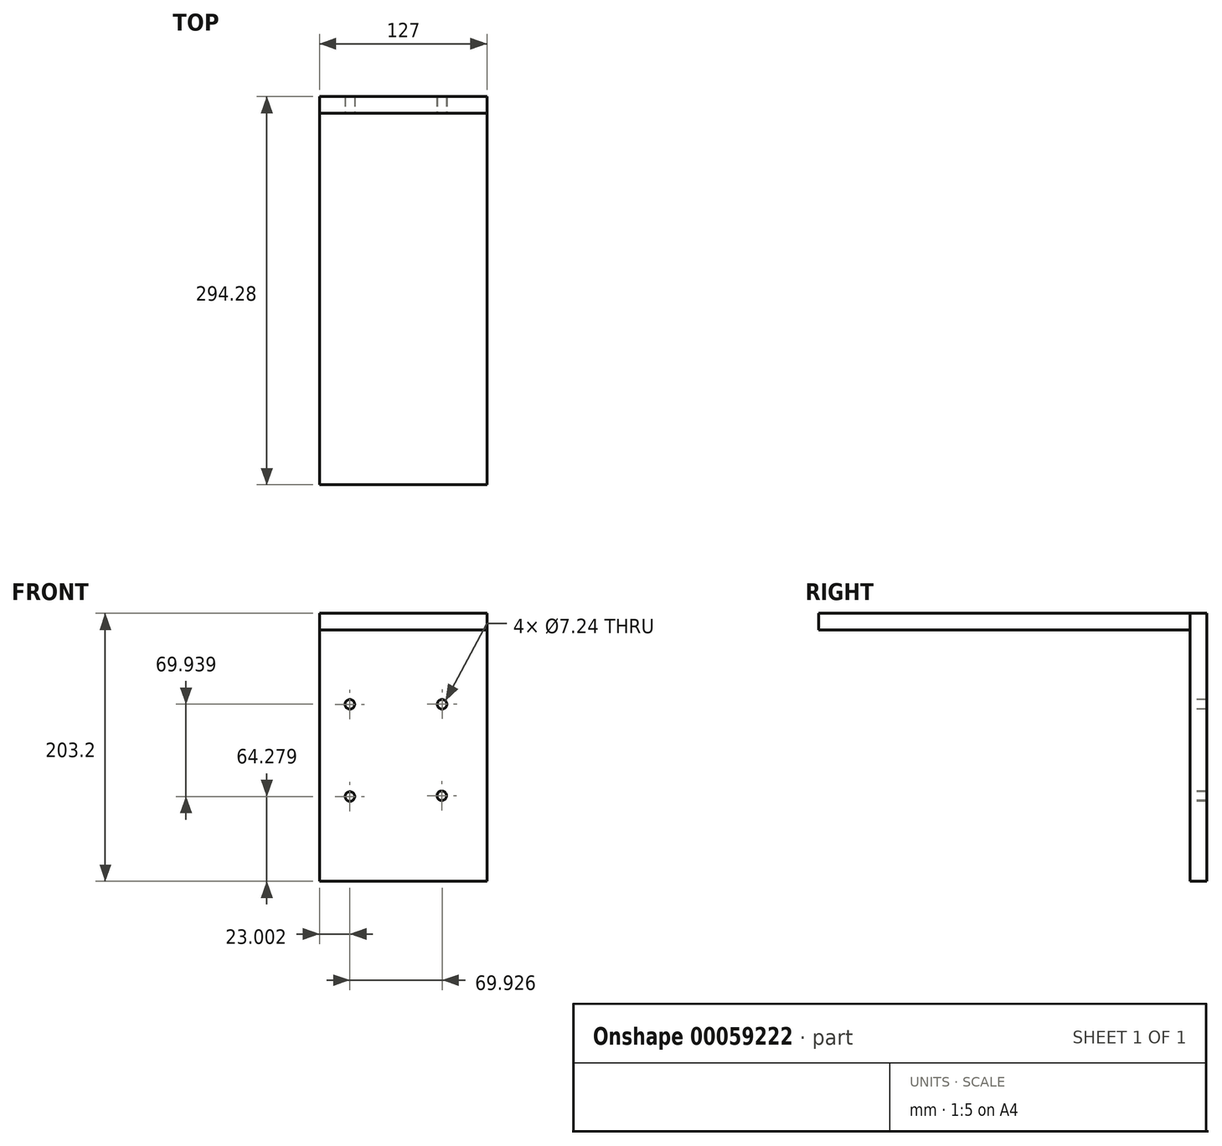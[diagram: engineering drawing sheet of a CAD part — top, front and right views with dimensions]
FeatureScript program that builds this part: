
annotation { "Feature Type Name" : "Feature", "Feature Type Description" : "" }
export const myFeature = defineFeature(function(context is Context, id is Id, definition is map)
    precondition{}
    {
        {
            var Q0;
            Q0=qCreatedBy(makeId("Front.planeOp"),FACE);
            var sketch = newSketch(context, id + "F0", { "sketchPlane" : qUnion([Q0])});
            skLineSegment(sketch, "E0.bottom", {"start": v(0, 0) * mm, "end": v(127, 0) * mm});
            skLineSegment(sketch, "E0.top", {"start": v(0, 203.2) * mm, "end": v(127, 203.2) * mm});
            skLineSegment(sketch, "E0.left", {"start": v(0, 0) * mm, "end": v(0, 203.2) * mm});
            skLineSegment(sketch, "E0.right", {"start": v(127, 0) * mm, "end": v(127, 203.2) * mm});
            skLineSegment(sketch, "E1.bottom", {"start": v(23.06, 134.13) * mm, "end": v(92.91, 134.13) * mm, "construction": true});
            skLineSegment(sketch, "E1.top", {"start": v(23.06, 64.28) * mm, "end": v(92.91, 64.28) * mm, "construction": true});
            skLineSegment(sketch, "E1.left", {"start": v(23.06, 134.13) * mm, "end": v(23.06, 64.28) * mm, "construction": true});
            skLineSegment(sketch, "E1.right", {"start": v(92.91, 134.13) * mm, "end": v(92.91, 64.28) * mm, "construction": true});
            skSolve(sketch);
        }
        {
            var Q0;
            Q0=makeQuery(id+"F0.imprint","IMPRINT",FACE,{"disambiguationData":[TD([[makeQuery(id+"F0.imprint","IMPRINT",EDGE,{"derivedFrom":sQuery(id+"F0.wireOp",EDGE,"E0.bottom")}),1.0]])]});
            extrude(context, id + "F1", {"entities" : qUnion([Q0]), "oppositeDirection" : true, "depth" : 12.7 * mm});
        }
        {
            var Q0;
            Q0=makeQuery(id+"F1.opExtrude","SWEPT_FACE",FACE,{"disambiguationData":[OSD([sQuery(id+"F0.wireOp",EDGE,"E0.top")])]});
            var sketch = newSketch(context, id + "F2", { "sketchPlane" : qUnion([Q0])});
            skLineSegment(sketch, "E2.bottom", {"start": v(0, 0) * mm, "end": v(127, 0) * mm});
            skLineSegment(sketch, "E2.top", {"start": v(0, -281.58) * mm, "end": v(127, -281.58) * mm});
            skLineSegment(sketch, "E2.left", {"start": v(0, 0) * mm, "end": v(0, -281.58) * mm});
            skLineSegment(sketch, "E2.right", {"start": v(127, 0) * mm, "end": v(127, -281.58) * mm});
            skSolve(sketch);
        }
        {
            var Q0;
            Q0=makeQuery(id+"F2.imprint","IMPRINT",FACE,{"disambiguationData":[TD([[makeQuery(id+"F2.imprint","IMPRINT",EDGE,{"derivedFrom":sQuery(id+"F2.wireOp",EDGE,"E2.bottom")}),-1.0]])]});
            extrude(context, id + "F3", {"entities" : qUnion([Q0]), "oppositeDirection" : true, "depth" : 12.7 * mm});
        }
        {
            var Q0;
            Q0=makeQuery(id+"F0.imprint","IMPRINT",FACE,{"disambiguationData":[TD([[makeQuery(id+"F0.imprint","IMPRINT",EDGE,{"derivedFrom":sQuery(id+"F0.wireOp",EDGE,"E0.bottom")}),1.0]])]});
            var sketch = newSketch(context, id + "F4", { "sketchPlane" : qUnion([Q0])});
            skCircle(sketch, "E3", {"center": v(92.69, 64.83) * mm, "radius": 3.62 * mm});
            skSolve(sketch);
        }
        {
            var Q0;
            Q0 = qSketchRegion(id + "F4", true);
            extrude(context, id + "F5", {"entities" : qUnion([Q0]), "operationType" : NewBodyOperationType.REMOVE, "oppositeDirection" : true, "depth" : 12.7 * mm});
        }
        {
            var Q0;
            Q0=makeQuery(id+"F0.imprint","IMPRINT",FACE,{"disambiguationData":[TD([[makeQuery(id+"F0.imprint","IMPRINT",EDGE,{"derivedFrom":sQuery(id+"F0.wireOp",EDGE,"E0.bottom")}),1.0]])]});
            var sketch = newSketch(context, id + "F6", { "sketchPlane" : qUnion([Q0])});
            skCircle(sketch, "E4", {"center": v(92.93, 134.22) * mm, "radius": 3.62 * mm});
            skSolve(sketch);
        }
        {
            var Q0;
            Q0 = qSketchRegion(id + "F6", true);
            extrude(context, id + "F7", {"entities" : qUnion([Q0]), "operationType" : NewBodyOperationType.REMOVE, "oppositeDirection" : true, "depth" : 12.7 * mm});
        }
        {
            var Q0;
            Q0=makeQuery(id+"F0.imprint","IMPRINT",FACE,{"disambiguationData":[TD([[makeQuery(id+"F0.imprint","IMPRINT",EDGE,{"derivedFrom":sQuery(id+"F0.wireOp",EDGE,"E0.bottom")}),1.0]])]});
            var sketch = newSketch(context, id + "F8", { "sketchPlane" : qUnion([Q0])});
            skCircle(sketch, "E5", {"center": v(23.06, 64.28) * mm, "radius": 3.62 * mm});
            skSolve(sketch);
        }
        {
            var Q0;
            Q0 = qSketchRegion(id + "F8", true);
            extrude(context, id + "F9", {"entities" : qUnion([Q0]), "operationType" : NewBodyOperationType.REMOVE, "oppositeDirection" : true, "depth" : 12.7 * mm});
        }
        {
            var Q0;
            Q0=makeQuery(id+"F0.imprint","IMPRINT",FACE,{"disambiguationData":[TD([[makeQuery(id+"F0.imprint","IMPRINT",EDGE,{"derivedFrom":sQuery(id+"F0.wireOp",EDGE,"E0.bottom")}),1.0]])]});
            var sketch = newSketch(context, id + "F10", { "sketchPlane" : qUnion([Q0])});
            skCircle(sketch, "E6", {"center": v(23, 134.16) * mm, "radius": 3.62 * mm});
            skSolve(sketch);
        }
        {
            var Q0;
            Q0 = qSketchRegion(id + "F10", true);
            extrude(context, id + "F11", {"entities" : qUnion([Q0]), "operationType" : NewBodyOperationType.REMOVE, "oppositeDirection" : true, "depth" : 12.7 * mm});
        }
    });
